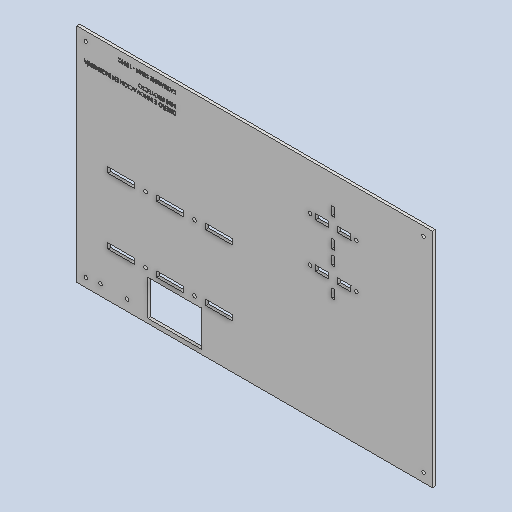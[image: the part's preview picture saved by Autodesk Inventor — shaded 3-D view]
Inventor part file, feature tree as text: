
AUTODESK INVENTOR PART (.ipt)
format: ipt  version: 2022 (Build 260153000, 153)  size: 1,056,768 bytes
history: native  units: mm
features: reference x75, other x8, sketch x4, extrude x3, emboss x1
ambient origin geometry x8: Origin, YZ Plane, XZ Plane, XY Plane, X Axis, Y Axis, Z Axis, Center Point
bodies: Solid1 (feature_tree)
feature tree (91):
  extrude  "Extrusion1"  Depth=250.0mm
  extrude  "Extrusion2"  Depth=3.2mm
  emboss  "Emboss1"
  extrude  "Extrusion3"  Depth=10.0mm TaperAngle=0.0deg
  sketch  "Sketch1"  dims[d0=400.0mm d1=250.0mm]
  sketch  "Sketch2"  dims[d2=3.2mm d3=0.0mm d4=4.0mm]
  reference  "Reference1"
  reference  "Reference2"
  reference  "Reference3"
  reference  "Reference4"
  reference  "Reference5"
  reference  "Reference6"
  reference  "Reference7"
  reference  "Reference8"
  reference  "Reference9"
  reference  "Reference10"
  reference  "Reference11"
  reference  "Reference12"
  reference  "Reference13"
  reference  "Reference14"
  reference  "Reference15"
  reference  "Reference16"
  reference  "Reference17"
  reference  "Reference18"
  reference  "Reference19"
  reference  "Reference20"
  reference  "Reference21"
  reference  "Reference22"
  reference  "Reference23"
  reference  "Reference24"
  reference  "Reference25"
  reference  "Reference26"
  reference  "Reference27"
  reference  "Reference28"
  reference  "Reference29"
  reference  "Reference30"
  reference  "Reference31"
  reference  "Reference32"
  reference  "Reference33"
  reference  "Reference34"
  reference  "Reference35"
  reference  "Reference36"
  reference  "Reference37"
  reference  "Reference38"
  reference  "Reference39"
  reference  "Reference40"
  reference  "Reference41"
  reference  "Reference42"
  reference  "Reference43"
  reference  "Reference44"
  reference  "Reference45"
  reference  "Reference46"
  reference  "Reference47"
  reference  "Reference48"
  reference  "Reference49"
  reference  "Reference50"
  reference  "Reference51"
  reference  "Reference52"
  reference  "Reference53"
  reference  "Reference54"
  reference  "Reference55"
  reference  "Reference56"
  reference  "Reference57"
  reference  "Reference58"
  reference  "Reference59"
  reference  "Reference60"
  reference  "Reference61"
  reference  "Reference62"
  reference  "Reference63"
  reference  "Reference64"
  reference  "Reference65"
  reference  "Reference66"
  reference  "Reference67"
  reference  "Reference68"
  reference  "Reference69"
  reference  "Reference70"
  reference  "Reference71"
  reference  "Reference72"
  reference  "Reference73"
  reference  "Reference74"
  sketch  "Sketch3"  dims[d5=4.0mm d6=10.0mm d7=0.0mm]
  sketch  "Sketch4"  dims[d8=0.1mm d9=0.0mm d10=60.0mm d11=40.0mm d12=5.0mm d13=80.0mm d14=15.0mm d15=0.0mm d16=4.0mm d17=15.0mm d18=10.0mm d19=4.0mm d20=10.0mm d21=10.0mm]
  reference  "Reference75"
  other  "Assembly_Final.iam"
  other  "Base:2"
  other  "Base:1"
  other  "Caja_Reductora:1"
  other  "Carcasa_CajaR_Lateral1:1"
  other  "Carcasa_CajaR_Lateral1:2"
  other  "Base_Soporte:2"
  other  "Acople_Motor:1"
